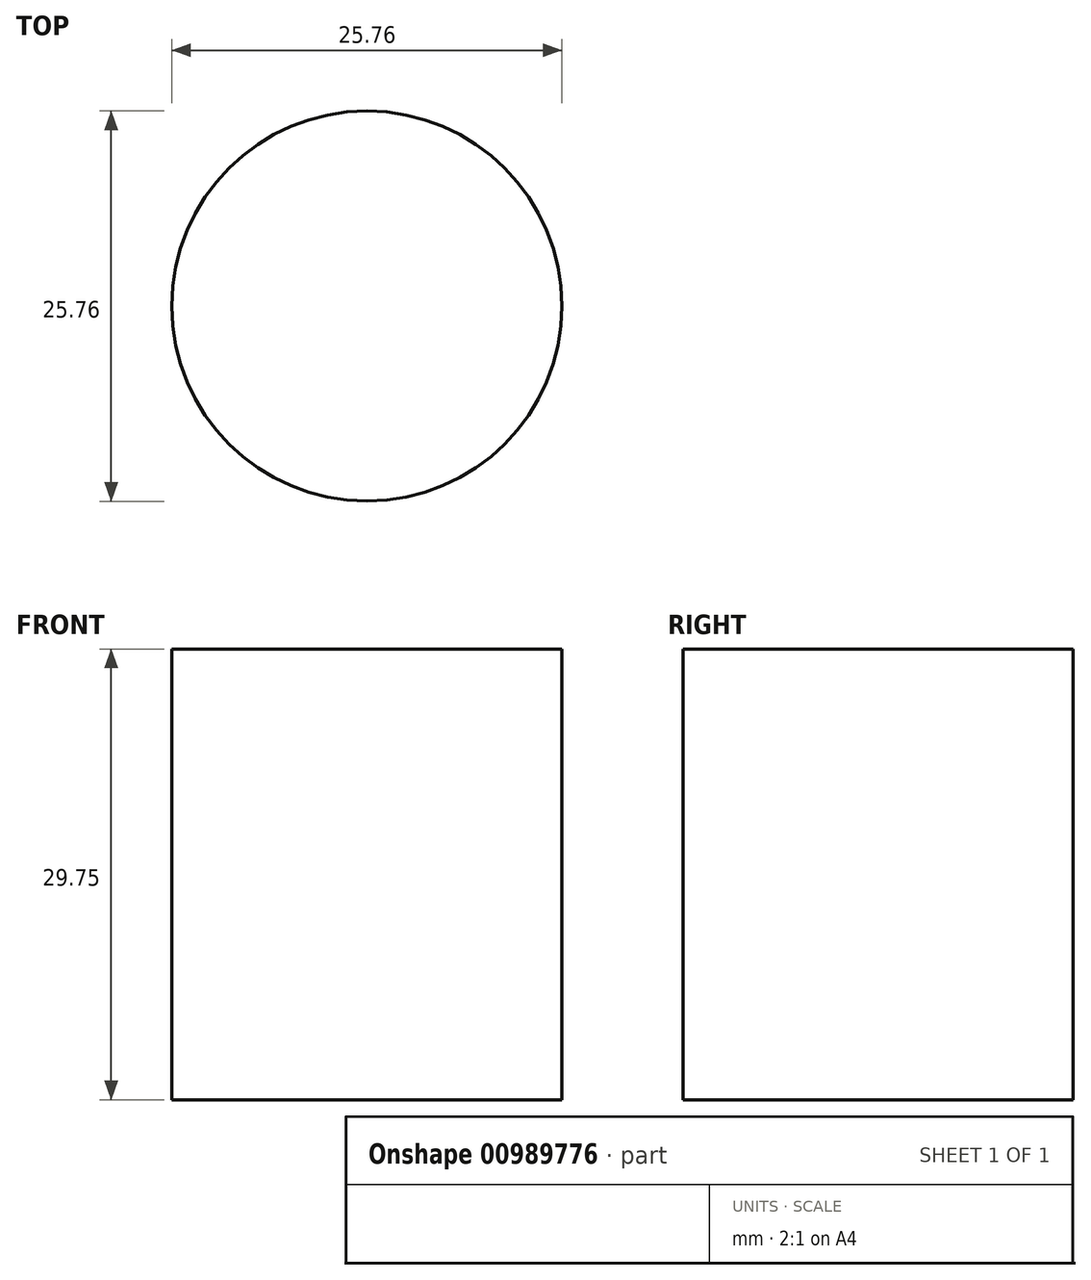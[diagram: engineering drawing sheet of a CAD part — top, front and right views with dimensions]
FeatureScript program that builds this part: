
annotation { "Feature Type Name" : "Feature", "Feature Type Description" : "" }
export const myFeature = defineFeature(function(context is Context, id is Id, definition is map)
    precondition{}
    {
        {
            var Q0;
            Q0=qCreatedBy(makeId("Top.planeOp"),FACE);
            var sketch = newSketch(context, id + "F0", { "sketchPlane" : qUnion([Q0])});
            skCircle(sketch, "E0", {"center": v(0, 0) * mm, "radius": 12.88 * mm});
            skSolve(sketch);
        }
        {
            var Q0;
            Q0 = qSketchRegion(id + "F0", true);
            extrude(context, id + "F1", {"entities" : qUnion([Q0]), "depth" : 29.75 * mm, "offsetDistance" : 25 * mm});
        }
    });
